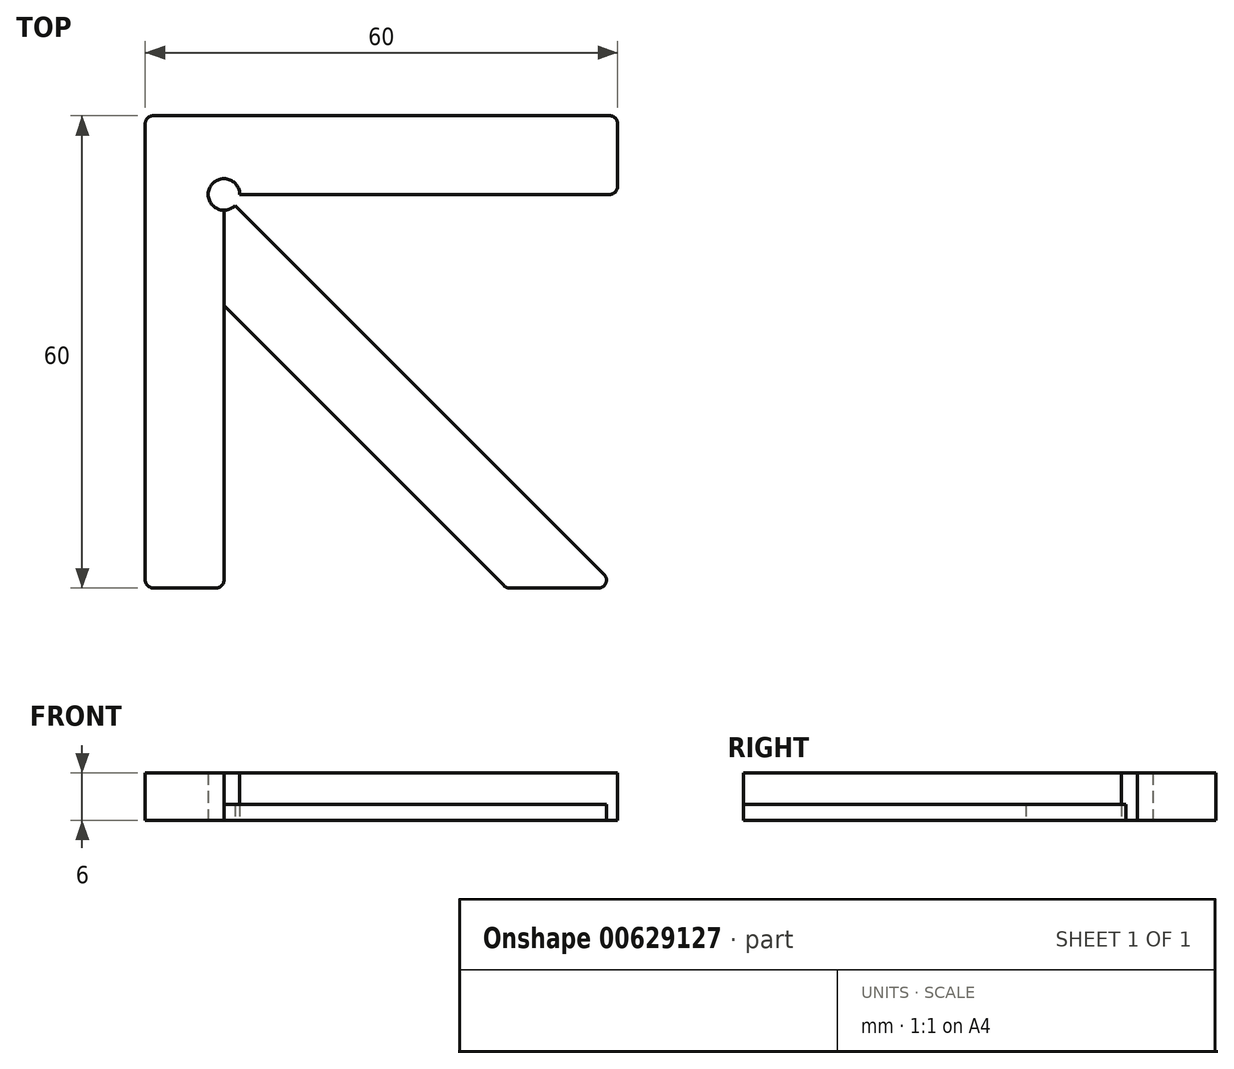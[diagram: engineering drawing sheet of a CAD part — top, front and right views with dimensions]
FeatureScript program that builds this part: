
annotation { "Feature Type Name" : "Feature", "Feature Type Description" : "" }
export const myFeature = defineFeature(function(context is Context, id is Id, definition is map)
    precondition{}
    {
        {
            var Q0;
            Q0=qCreatedBy(makeId("Top.planeOp"),FACE);
            var sketch = newSketch(context, id + "F0", { "sketchPlane" : qUnion([Q0])});
            skLineSegment(sketch, "E0", {"start": v(2, 0) * mm, "end": v(50, 0) * mm});
            skLineSegment(sketch, "E1", {"start": v(50, 0) * mm, "end": v(50, 10) * mm});
            skLineSegment(sketch, "E2", {"start": v(50, 10) * mm, "end": v(-10, 10) * mm});
            skLineSegment(sketch, "E3", {"start": v(-10, 10) * mm, "end": v(-10, -50) * mm});
            skLineSegment(sketch, "E4", {"start": v(-10, -50) * mm, "end": v(0, -50) * mm});
            skLineSegment(sketch, "E5", {"start": v(0, -50) * mm, "end": v(0, -2) * mm});
            skLineSegment(sketch, "E6", {"start": v(1.41, -1.41) * mm, "end": v(50, -50) * mm});
            skLineSegment(sketch, "E7", {"start": v(50, -50) * mm, "end": v(35.86, -50) * mm});
            skLineSegment(sketch, "E8", {"start": v(35.86, -50) * mm, "end": v(0, -14.14) * mm});
            skArc(sketch, "E9", {"start": v(2, 0) * mm, "mid": v(-1.85, 0.77) * mm, "end": v(1.41, -1.41) * mm});
            skSolve(sketch);
        }
        {
            var Q0;
            Q0 = qSketchRegion(id + "F0", true);
            extrude(context, id + "F1", {"entities" : qUnion([Q0]), "depth" : 2 * mm, "offsetDistance" : 25 * mm});
        }
        {
            var Q0;
            {var subQ0=sQuery(id+"F0.wireOp",EDGE,"E0");Q0=makeQuery(id+"F0.imprint","IMPRINT",FACE,{"disambiguationData":[TD([[makeQuery(id+"F0.imprint","IMPRINT",EDGE,{"derivedFrom":subQ0}),1.0]])]});}
            extrude(context, id + "F2", {"entities" : qUnion([Q0]), "operationType" : NewBodyOperationType.ADD, "depth" : 6 * mm, "offsetDistance" : 25 * mm});
        }
        {
            var Q0;
            {var subQ0=sQuery(id+"F0.wireOp",EDGE,"E4");var subQ1=sQuery(id+"F0.wireOp",EDGE,"E3");Q0=makeQuery(id+"F2.boolean.opBoolean","MERGE",EDGE,{"derivedFrom":[makeQuery(id+"F1.opExtrude","SWEPT_EDGE",EDGE,{"disambiguationData":[OSD([subQ1,subQ0])]}),makeQuery(id+"F2.opExtrude","SWEPT_EDGE",EDGE,{"disambiguationData":[OSD([subQ1,subQ0])]})]});}
            var Q1;
            {var subQ0=sQuery(id+"F0.wireOp",EDGE,"E5");var subQ1=sQuery(id+"F0.wireOp",EDGE,"E4");Q1=makeQuery(id+"F2.boolean.opBoolean","MERGE",EDGE,{"derivedFrom":[makeQuery(id+"F1.opExtrude","SWEPT_EDGE",EDGE,{"disambiguationData":[OSD([subQ1,subQ0])]}),makeQuery(id+"F2.opExtrude","SWEPT_EDGE",EDGE,{"disambiguationData":[OSD([subQ1,subQ0])]})]});}
            var Q2;
            Q2=makeQuery(id+"F1.opExtrude","SWEPT_EDGE",EDGE,{"disambiguationData":[OSD([sQuery(id+"F0.wireOp",EDGE,"E7"),sQuery(id+"F0.wireOp",EDGE,"E8")])]});
            var Q3;
            {var subQ0=sQuery(id+"F0.wireOp",EDGE,"E1");var subQ1=sQuery(id+"F0.wireOp",EDGE,"E0");Q3=makeQuery(id+"F2.boolean.opBoolean","MERGE",EDGE,{"derivedFrom":[makeQuery(id+"F1.opExtrude","SWEPT_EDGE",EDGE,{"disambiguationData":[OSD([subQ1,subQ0])]}),makeQuery(id+"F2.opExtrude","SWEPT_EDGE",EDGE,{"disambiguationData":[OSD([subQ1,subQ0])]})]});}
            var Q4;
            {var subQ0=sQuery(id+"F0.wireOp",EDGE,"E2");var subQ1=sQuery(id+"F0.wireOp",EDGE,"E1");Q4=makeQuery(id+"F2.boolean.opBoolean","MERGE",EDGE,{"derivedFrom":[makeQuery(id+"F1.opExtrude","SWEPT_EDGE",EDGE,{"disambiguationData":[OSD([subQ1,subQ0])]}),makeQuery(id+"F2.opExtrude","SWEPT_EDGE",EDGE,{"disambiguationData":[OSD([subQ1,subQ0])]})]});}
            var Q5;
            {var subQ0=sQuery(id+"F0.wireOp",EDGE,"E3");var subQ1=sQuery(id+"F0.wireOp",EDGE,"E2");Q5=makeQuery(id+"F2.boolean.opBoolean","MERGE",EDGE,{"derivedFrom":[makeQuery(id+"F1.opExtrude","SWEPT_EDGE",EDGE,{"disambiguationData":[OSD([subQ1,subQ0])]}),makeQuery(id+"F2.opExtrude","SWEPT_EDGE",EDGE,{"disambiguationData":[OSD([subQ1,subQ0])]})]});}
            var Q6;
            Q6=makeQuery(id+"F1.opExtrude","SWEPT_EDGE",EDGE,{"disambiguationData":[OSD([sQuery(id+"F0.wireOp",EDGE,"E6"),sQuery(id+"F0.wireOp",EDGE,"E7")])]});
            fillet(context, id + "F3", {"entities" : qUnion([Q0, Q1, Q2, Q3, Q4, Q5, Q6]), "radius" : 1 * mm, "tangentPropagation" : true, "allowEdgeOverflow" : false});
        }
        {
            var Q0;
            Q0=makeQuery(id+"F1.opExtrude","SWEPT_BODY",BODY,{"disambiguationData":[OSD([sQuery(id+"F0.wireOp",EDGE,"E0"),sQuery(id+"F0.wireOp",EDGE,"E1"),sQuery(id+"F0.wireOp",EDGE,"E2"),sQuery(id+"F0.wireOp",EDGE,"E3"),sQuery(id+"F0.wireOp",EDGE,"E4"),sQuery(id+"F0.wireOp",EDGE,"E5"),sQuery(id+"F0.wireOp",EDGE,"E6"),sQuery(id+"F0.wireOp",EDGE,"E7"),sQuery(id+"F0.wireOp",EDGE,"E8"),sQuery(id+"F0.wireOp",EDGE,"E9")])]});
            transform(context, id + "F4", {"entities" : qUnion([Q0]), "transformType" : TransformType.TRANSLATION_3D, "dx" : -10.7 * mm, "dy" : 11.9 * mm, "dz" : 0 * mm, "makeCopy" : false});
        }
    });
